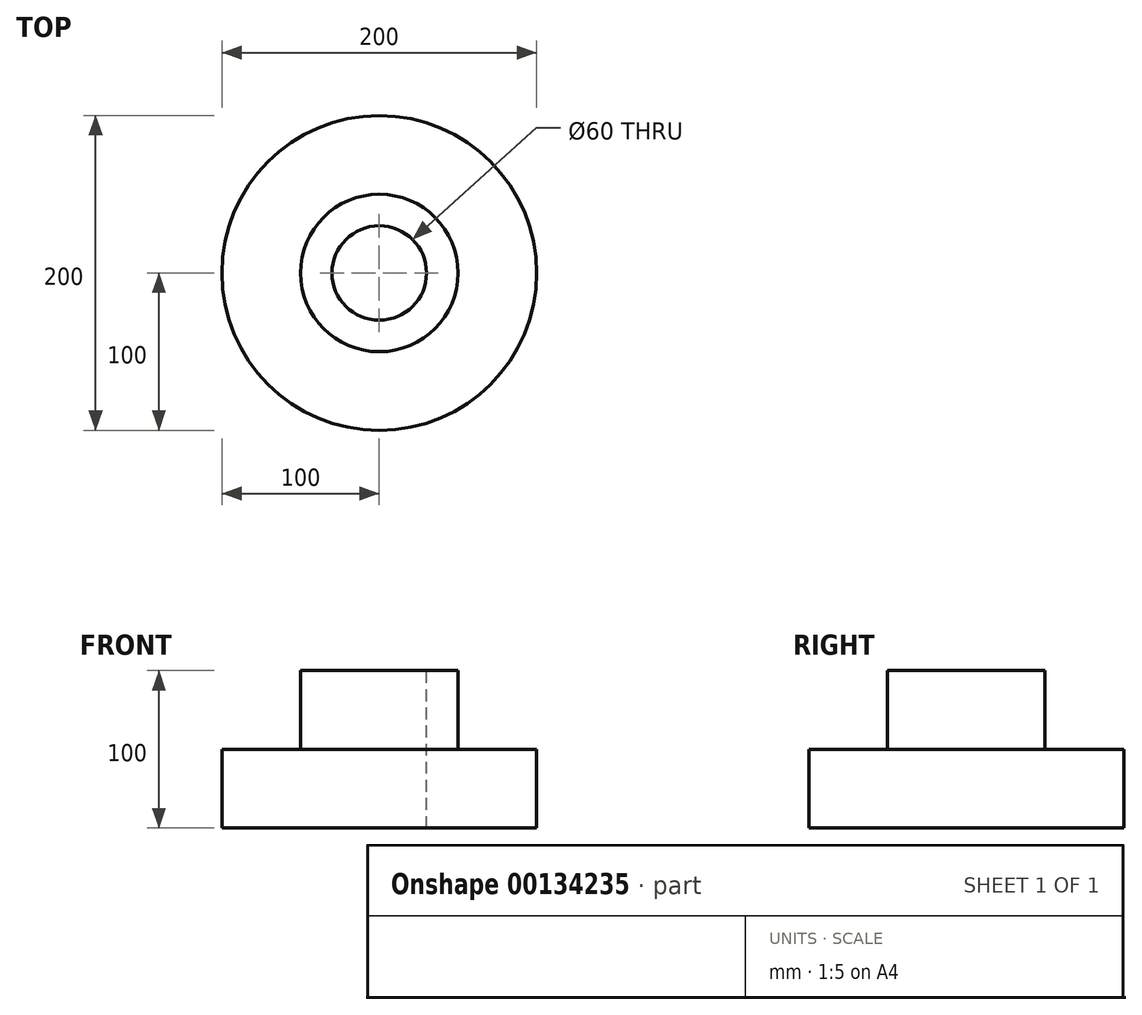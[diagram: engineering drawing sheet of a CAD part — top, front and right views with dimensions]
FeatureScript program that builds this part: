
annotation { "Feature Type Name" : "Feature", "Feature Type Description" : "" }
export const myFeature = defineFeature(function(context is Context, id is Id, definition is map)
    precondition{}
    {
        {
            var Q0;
            Q0=qCreatedBy(makeId("Front.planeOp"),FACE);
            var sketch = newSketch(context, id + "F0", { "sketchPlane" : qUnion([Q0])});
            skLineSegment(sketch, "E0", {"start": v(0, 0) * mm, "end": v(100, 0) * mm});
            skLineSegment(sketch, "E1", {"start": v(100, 0) * mm, "end": v(100, 50) * mm});
            skLineSegment(sketch, "E2", {"start": v(100, 50) * mm, "end": v(50, 50) * mm});
            skLineSegment(sketch, "E3", {"start": v(50, 50) * mm, "end": v(50, 100) * mm});
            skLineSegment(sketch, "E4", {"start": v(50, 100) * mm, "end": v(0, 100) * mm});
            skLineSegment(sketch, "E5", {"start": v(0, 100) * mm, "end": v(0, 0) * mm});
            skSolve(sketch);
        }
        {
            var Q0;
            Q0=makeQuery(id+"F0.imprint","IMPRINT",FACE,{"disambiguationData":[TD([[makeQuery(id+"F0.imprint","IMPRINT",EDGE,{"derivedFrom":sQuery(id+"F0.wireOp",EDGE,"E0")}),1.0]])]});
            var Q1;
            Q1=sQuery(id+"F0.wireOp",EDGE,"E5");
            revolve(context, id + "F1", {"entities" : qUnion([Q0]), "axis" : qUnion([Q1]), "revolveType" : RevolveType.FULL});
        }
        {
            var Q0;
            Q0=makeQuery(id+"F1.opRevolve","SWEPT_FACE",FACE,{"disambiguationData":[OSD([sQuery(id+"F0.wireOp",EDGE,"E4")])]});
            var sketch = newSketch(context, id + "F2", { "sketchPlane" : qUnion([Q0])});
            skPoint(sketch, "E6", {"position": v(0, 0) * mm});
            skSolve(sketch);
        }
        {
            var Q0;
            Q0=sQuery(id+"F2.wireOp",VERTEX,"E6");
            var Q1;
            Q1=makeQuery(id+"F1.opRevolve","SWEPT_BODY",BODY,{"disambiguationData":[OSD([sQuery(id+"F0.wireOp",EDGE,"E0"),sQuery(id+"F0.wireOp",EDGE,"E1"),sQuery(id+"F0.wireOp",EDGE,"E2"),sQuery(id+"F0.wireOp",EDGE,"E3"),sQuery(id+"F0.wireOp",EDGE,"E4"),sQuery(id+"F0.wireOp",EDGE,"E5")])]});
            hole(context, id + "F3", {"style" : HoleStyle.SIMPLE, "endStyle" : HoleEndStyle.THROUGH, "holeDiameter" : 60 * mm, "locations" : qUnion([Q0]), "scope" : qUnion([Q1]), "isTappedThrough" : true});
        }
    });
